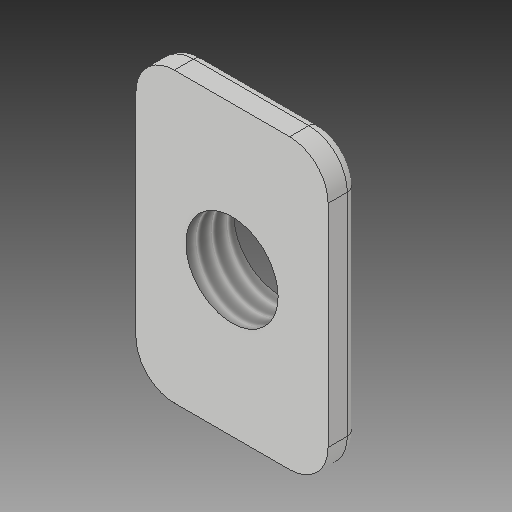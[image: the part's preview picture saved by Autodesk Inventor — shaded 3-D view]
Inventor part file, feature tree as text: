
AUTODESK INVENTOR PART (.ipt)
format: ipt  version: 2017 (Build 210142000, 142)  size: 156,672 bytes
history: native  units: mm
features: other x3, sketch x2
ambient origin geometry x8: Origin, YZ Plane, XZ Plane, XY Plane, X Axis, Y Axis, Z Axis, Center Point
bodies: Solid1 (feature_tree)
feature tree (5):
  other  "M5 Tee Nut-Generic.ipt"
  other  "Solid1::M5 Tee Nut-Generic.ipt"
  other  "TaggingFeature1"
  sketch  "Sketch1"  dims[d0=10.0mm]
  sketch  "Sketch2"
